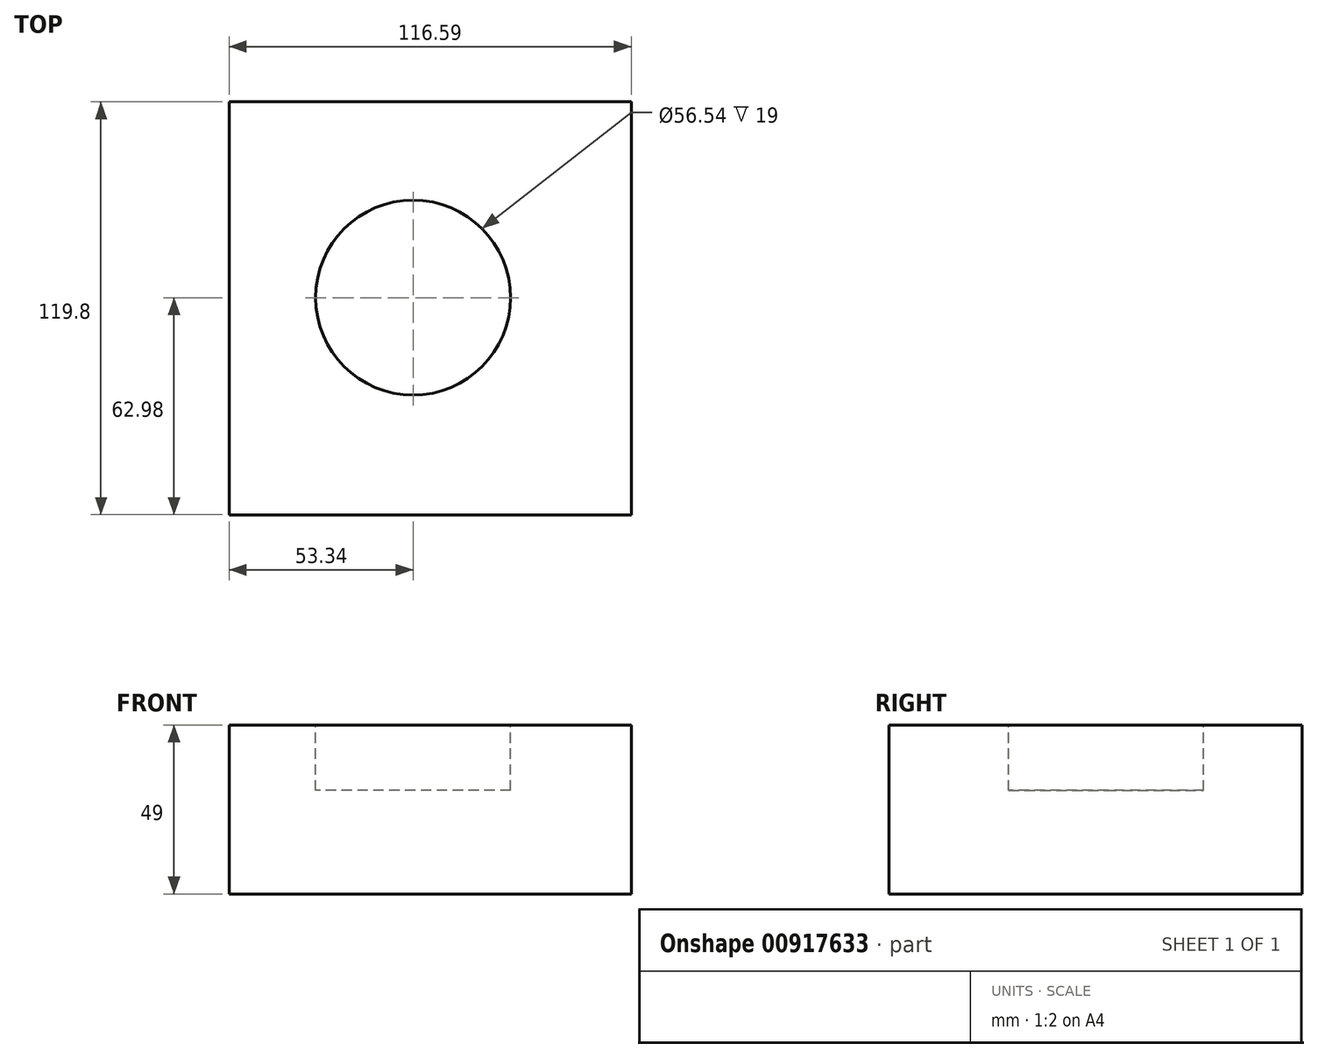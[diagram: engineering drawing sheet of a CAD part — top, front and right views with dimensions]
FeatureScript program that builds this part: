
annotation { "Feature Type Name" : "Feature", "Feature Type Description" : "" }
export const myFeature = defineFeature(function(context is Context, id is Id, definition is map)
    precondition{}
    {
        {
            var Q0;
            Q0=qCreatedBy(makeId("Top.planeOp"),FACE);
            var sketch = newSketch(context, id + "F0", { "sketchPlane" : qUnion([Q0])});
            skLineSegment(sketch, "E0.bottom", {"start": v(-53.34, -62.98) * mm, "end": v(63.25, -62.98) * mm});
            skLineSegment(sketch, "E0.top", {"start": v(-53.34, 56.82) * mm, "end": v(63.25, 56.82) * mm});
            skLineSegment(sketch, "E0.left", {"start": v(-53.34, -62.98) * mm, "end": v(-53.34, 56.82) * mm});
            skLineSegment(sketch, "E0.right", {"start": v(63.25, -62.98) * mm, "end": v(63.25, 56.82) * mm});
            skCircle(sketch, "E1", {"center": v(0, 0) * mm, "radius": 28.27 * mm});
            skSolve(sketch);
        }
        {
            var Q0;
            Q0=makeQuery(id+"F0.imprint","IMPRINT",FACE,{"disambiguationData":[TD([[makeQuery(id+"F0.imprint","IMPRINT",EDGE,{"derivedFrom":sQuery(id+"F0.wireOp",EDGE,"E0.bottom")}),1.0]])]});
            var Q1;
            Q1=makeQuery(id+"F0.imprint","IMPRINT",FACE,{"disambiguationData":[TD([[makeQuery(id+"F0.imprint","IMPRINT",EDGE,{"derivedFrom":sQuery(id+"F0.wireOp",EDGE,"E1")}),1.0]])]});
            extrude(context, id + "F1", {"entities" : qUnion([Q0, Q1]), "oppositeDirection" : true, "depth" : 49 * mm, "offsetDistance" : 25 * mm});
        }
        {
            var Q0;
            Q0=makeQuery(id+"F0.imprint","IMPRINT",FACE,{"disambiguationData":[TD([[makeQuery(id+"F0.imprint","IMPRINT",EDGE,{"derivedFrom":sQuery(id+"F0.wireOp",EDGE,"E1")}),1.0]])]});
            extrude(context, id + "F2", {"entities" : qUnion([Q0]), "operationType" : NewBodyOperationType.REMOVE, "oppositeDirection" : true, "depth" : 19 * mm, "offsetDistance" : 25 * mm});
        }
    });
